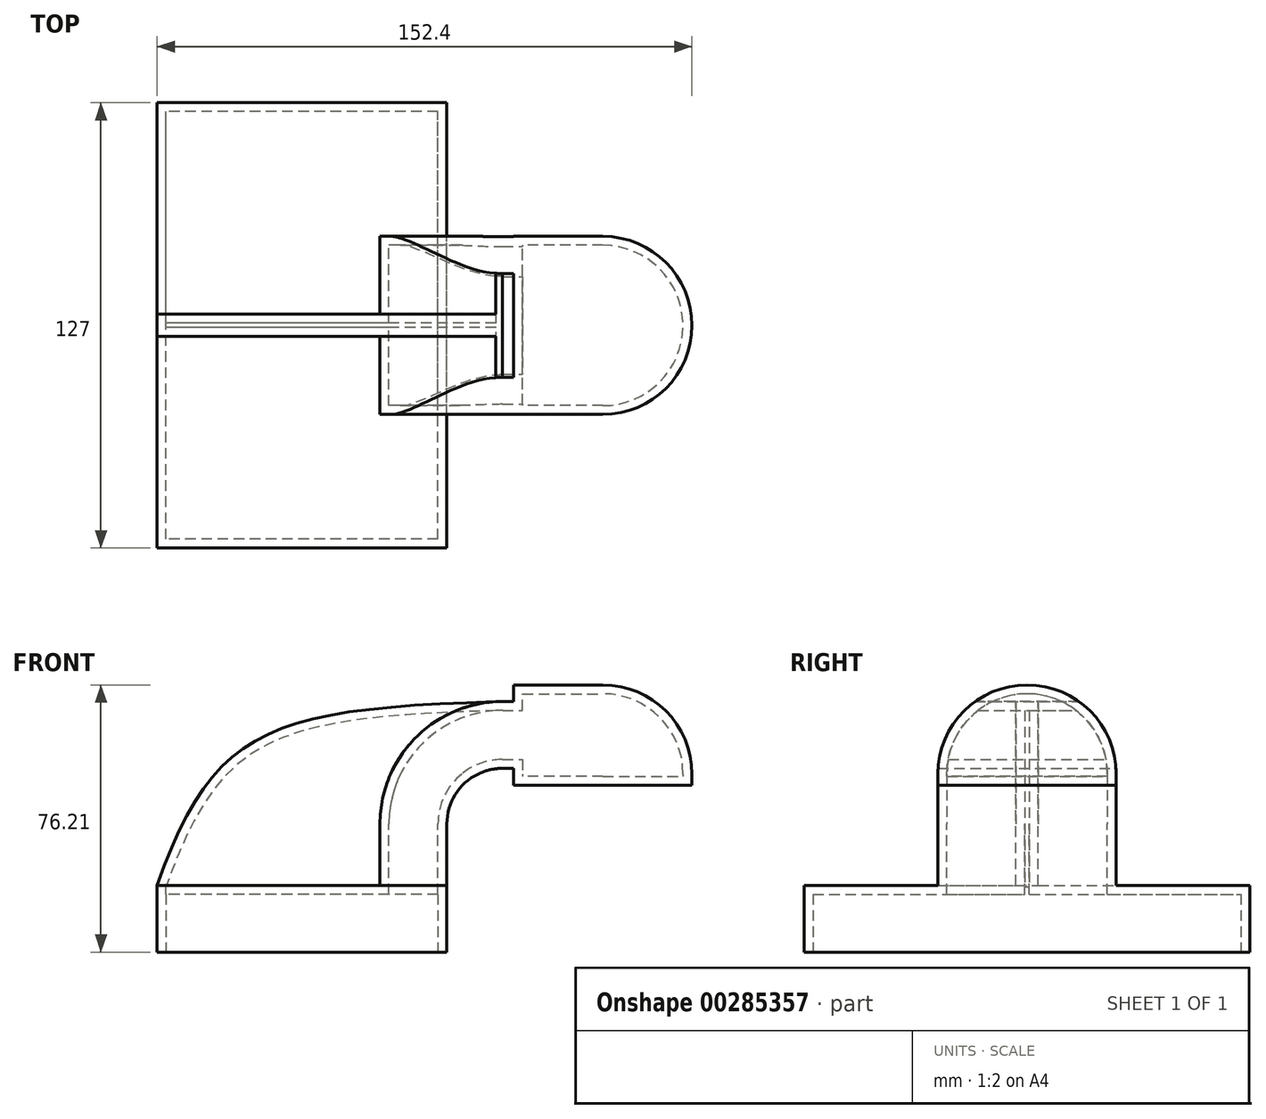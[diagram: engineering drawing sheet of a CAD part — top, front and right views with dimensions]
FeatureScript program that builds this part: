
annotation { "Feature Type Name" : "Feature", "Feature Type Description" : "" }
export const myFeature = defineFeature(function(context is Context, id is Id, definition is map)
    precondition{}
    {
        {
            var Q0;
            Q0=qCreatedBy(makeId("Front.planeOp"),FACE);
            var sketch = newSketch(context, id + "F0", { "sketchPlane" : qUnion([Q0])});
            skLineSegment(sketch, "E0.bottom", {"start": v(41.27, 9.53) * mm, "end": v(-41.27, 9.53) * mm});
            skLineSegment(sketch, "E0.top", {"start": v(41.28, -9.52) * mm, "end": v(-41.27, -9.52) * mm});
            skLineSegment(sketch, "E0.left", {"start": v(41.28, 9.53) * mm, "end": v(41.28, -9.52) * mm});
            skLineSegment(sketch, "E0.right", {"start": v(-41.27, 9.53) * mm, "end": v(-41.27, -9.52) * mm});
            skPoint(sketch, "E0.middle", {"position": v(0, 0) * mm});
            skLineSegment(sketch, "E1.bottom", {"start": v(111.12, 66.68) * mm, "end": v(60.32, 66.68) * mm});
            skLineSegment(sketch, "E1.top", {"start": v(111.12, 38.1) * mm, "end": v(60.32, 38.1) * mm});
            skLineSegment(sketch, "E1.left", {"start": v(111.12, 66.68) * mm, "end": v(111.12, 38.1) * mm});
            skLineSegment(sketch, "E1.right", {"start": v(60.32, 66.68) * mm, "end": v(60.32, 38.1) * mm});
            skPoint(sketch, "E1.middle", {"position": v(85.72, 52.39) * mm});
            skLineSegment(sketch, "E2", {"start": v(41.27, 9.53) * mm, "end": v(41.27, 27) * mm});
            skArc(sketch, "E3", {"start": v(41.27, 27) * mm, "mid": v(45.92, 38.23) * mm, "end": v(57.15, 42.88) * mm});
            skLineSegment(sketch, "E4", {"start": v(57.15, 42.88) * mm, "end": v(85.72, 42.88) * mm});
            skLineSegment(sketch, "E5.0", {"start": v(57.15, 61.93) * mm, "end": v(85.72, 61.93) * mm});
            skArc(sketch, "E5.1", {"start": v(22.22, 27) * mm, "mid": v(32.45, 51.7) * mm, "end": v(57.15, 61.93) * mm});
            skLineSegment(sketch, "E5.2", {"start": v(22.22, 9.53) * mm, "end": v(22.22, 27) * mm});
            skLineSegment(sketch, "E6", {"start": v(85.72, 38.1) * mm, "end": v(85.72, 66.68) * mm});
            skFitSpline(sketch, "E7", {"points": [v(-41.28, 9.53) * mm, v(57.15, 61.93) * mm], "startDerivative": vector(47.34, 134.57) * mm, "endDerivative": vector(200.4, 5.47) * mm});
            skSolve(sketch);
        }
        {
            var Q0;
            Q0=makeQuery(id+"F0.imprint","IMPRINT",FACE,{"disambiguationData":[TD([[makeQuery(id+"F0.imprint","IMPRINT",EDGE,{"derivedFrom":sQuery(id+"F0.wireOp",EDGE,"E0.top")}),-1.0]])]});
            extrude(context, id + "F1", {"entities" : qUnion([Q0]), "endBound" : BoundingType.SYMMETRIC, "depth" : 127 * mm});
        }
        {
            var Q0;
            {var subQ1=sQuery(id+"F0.wireOp",EDGE,"E2");Q0=makeQuery(id+"F0.imprint","IMPRINT",FACE,{"disambiguationData":[TD([[makeQuery(id+"F0.imprint","IMPRINT",EDGE,{"derivedFrom":subQ1}),1.0]])]});}
            var Q1;
            {var subQ0=sQuery(id+"F0.wireOp",EDGE,"E5.0");var subQ1=sQuery(id+"F0.wireOp",EDGE,"E1.right");var subQ2=makeQuery(id+"F0.imprint","INTERSECT",VERTEX,{"derivedFrom":[subQ1,subQ0]});Q1=makeQuery(id+"F0.imprint","IMPRINT",FACE,{"disambiguationData":[TD([[makeQuery(id+"F0.imprint","IMPRINT",EDGE,{"disambiguationData":[TD([[subQ2,-1.0]])],"derivedFrom":subQ1}),1.0]])]});}
            var Q2;
            {var subQ0=sQuery(id+"F0.wireOp",EDGE,"E1.right");var subQ1=sQuery(id+"F0.wireOp",EDGE,"E1.top");var subQ2=makeQuery(id+"F0.imprint","INTERSECT",VERTEX,{"derivedFrom":[subQ1,subQ0]});Q2=makeQuery(id+"F0.imprint","IMPRINT",FACE,{"disambiguationData":[TD([[makeQuery(id+"F0.imprint","IMPRINT",EDGE,{"disambiguationData":[TD([[subQ2,1.0]])],"derivedFrom":subQ1}),-1.0]])]});}
            var Q3;
            {var subQ0=sQuery(id+"F0.wireOp",EDGE,"E1.right");var subQ1=sQuery(id+"F0.wireOp",EDGE,"E1.bottom");var subQ2=makeQuery(id+"F0.imprint","INTERSECT",VERTEX,{"derivedFrom":[subQ1,subQ0]});Q3=makeQuery(id+"F0.imprint","IMPRINT",FACE,{"disambiguationData":[TD([[makeQuery(id+"F0.imprint","IMPRINT",EDGE,{"disambiguationData":[TD([[subQ2,1.0]])],"derivedFrom":subQ1}),1.0]])]});}
            extrude(context, id + "F2", {"entities" : qUnion([Q0, Q1, Q2, Q3]), "operationType" : NewBodyOperationType.ADD, "endBound" : BoundingType.SYMMETRIC, "depth" : 50.8 * mm});
        }
        {
            var Q0;
            {var subQ3=sQuery(id+"F0.wireOp",EDGE,"E5.2");Q0=makeQuery(id+"F0.imprint","IMPRINT",FACE,{"disambiguationData":[TD([[makeQuery(id+"F0.imprint","IMPRINT",EDGE,{"derivedFrom":subQ3}),1.0]])]});}
            extrude(context, id + "F3", {"entities" : qUnion([Q0]), "operationType" : NewBodyOperationType.ADD, "endBound" : BoundingType.SYMMETRIC, "depth" : 6.35 * mm});
        }
        {
            var Q0;
            {var subQ0=sQuery(id+"F0.wireOp",EDGE,"E1.left");Q0=makeQuery(id+"F0.imprint","IMPRINT",FACE,{"disambiguationData":[TD([[makeQuery(id+"F0.imprint","IMPRINT",EDGE,{"derivedFrom":subQ0}),-1.0]])]});}
            var Q1;
            Q1=sQuery(id+"F0.wireOp",EDGE,"E6");
            revolve(context, id + "F4", {"operationType" : NewBodyOperationType.ADD, "entities" : qUnion([Q0]), "axis" : qUnion([Q1]), "revolveType" : RevolveType.FULL});
        }
        {
            var Q0;
            Q0=makeQuery(id+"F4.opRevolve","SWEPT_EDGE",EDGE,{"disambiguationData":[OSD([sQuery(id+"F0.wireOp",EDGE,"E1.bottom"),sQuery(id+"F0.wireOp",EDGE,"E1.left")])]});
            fillet(context, id + "F5", {"entities" : qUnion([Q0]), "radius" : 25.4 * mm, "tangentPropagation" : true, "allowEdgeOverflow" : false});
        }
        {
            var Q0;
            Q0=makeQuery(id+"F1.opExtrude","SWEPT_FACE",FACE,{"disambiguationData":[OSD([sQuery(id+"F0.wireOp",EDGE,"E0.top")])]});
            shell(context, id + "F6", {"entities" : qUnion([Q0]), "thickness" : 2.54 * mm});
        }
    });
